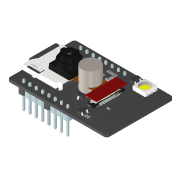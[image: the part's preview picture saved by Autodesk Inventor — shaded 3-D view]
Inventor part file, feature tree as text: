
AUTODESK INVENTOR PART (.ipt)
format: ipt  version: 2022 (Build 260153000, 153)  size: 4,575,232 bytes
history: native  units: mm
features: other x110, extrude x1, sketch x1, projected_geometry x1
ambient origin geometry x8: Origin, YZ Plane, XZ Plane, XY Plane, X Axis, Y Axis, Z Axis, Center Point
bodies: Volumenkörper1 (feature_tree), Volumenkörper2 (feature_tree), Volumenkörper3 (feature_tree), Volumenkörper4 (feature_tree), Volumenkörper5 (feature_tree), Volumenkörper6 (feature_tree), Volumenkörper7 (feature_tree), Volumenkörper8 (feature_tree), Volumenkörper9 (feature_tree), Volumenkörper10 (feature_tree), Volumenkörper11 (feature_tree), Volumenkörper12 (feature_tree), Volumenkörper13 (feature_tree), Volumenkörper14 (feature_tree), Volumenkörper15 (feature_tree), Volumenkörper16 (feature_tree), Volumenkörper17 (feature_tree), Volumenkörper18 (feature_tree), Volumenkörper19 (feature_tree), Volumenkörper20 (feature_tree), Volumenkörper21 (feature_tree), Volumenkörper22 (feature_tree), Volumenkörper23 (feature_tree), Volumenkörper24 (feature_tree), Volumenkörper25 (feature_tree), Volumenkörper26 (feature_tree), Volumenkörper27 (feature_tree), Volumenkörper28 (feature_tree), Volumenkörper29 (feature_tree), Volumenkörper30 (feature_tree), Volumenkörper31 (feature_tree), Volumenkörper32 (feature_tree), Volumenkörper33 (feature_tree), Volumenkörper34 (feature_tree), Volumenkörper35 (feature_tree), Volumenkörper36 (feature_tree), Volumenkörper37 (feature_tree), Volumenkörper38 (feature_tree), Volumenkörper39 (feature_tree), Volumenkörper40 (feature_tree), Volumenkörper41 (feature_tree), Volumenkörper42 (feature_tree), Volumenkörper43 (feature_tree), Volumenkörper44 (feature_tree), Volumenkörper45 (feature_tree), Volumenkörper46 (feature_tree), Volumenkörper47 (feature_tree), Volumenkörper48 (feature_tree), Volumenkörper49 (feature_tree), Volumenkörper50 (feature_tree), Volumenkörper51 (feature_tree), Volumenkörper52 (feature_tree), Volumenkörper53 (feature_tree), Volumenkörper54 (feature_tree), Volumenkörper55 (feature_tree), Volumenkörper56 (feature_tree), Volumenkörper57 (feature_tree), Volumenkörper58 (feature_tree), Volumenkörper59 (feature_tree), Volumenkörper60 (feature_tree), Volumenkörper61 (feature_tree), Volumenkörper62 (feature_tree), Volumenkörper63 (feature_tree), Volumenkörper64 (feature_tree), Volumenkörper65 (feature_tree), Volumenkörper66 (feature_tree), Volumenkörper67 (feature_tree), Volumenkörper68 (feature_tree), Volumenkörper69 (feature_tree), Volumenkörper70 (feature_tree), Volumenkörper71 (feature_tree), Volumenkörper72 (feature_tree), Volumenkörper73 (feature_tree), Volumenkörper74 (feature_tree), Volumenkörper75 (feature_tree), Volumenkörper76 (feature_tree), Volumenkörper77 (feature_tree), Volumenkörper78 (feature_tree), Volumenkörper79 (feature_tree), Volumenkörper80 (feature_tree), Volumenkörper81 (feature_tree), Volumenkörper82 (feature_tree), Volumenkörper83 (feature_tree), Volumenkörper84 (feature_tree), Volumenkörper85 (feature_tree), Volumenkörper86 (feature_tree), Volumenkörper87 (feature_tree), Volumenkörper88 (feature_tree), Volumenkörper89 (feature_tree), Volumenkörper90 (feature_tree), Volumenkörper91 (feature_tree), Volumenkörper92 (feature_tree), Volumenkörper93 (feature_tree), Volumenkörper94 (feature_tree), Volumenkörper95 (feature_tree), Volumenkörper96 (feature_tree), Volumenkörper97 (feature_tree), Volumenkörper98 (feature_tree), Volumenkörper99 (feature_tree), Volumenkörper100 (feature_tree), Volumenkörper101 (feature_tree), Volumenkörper102 (feature_tree), Volumenkörper103 (feature_tree), Volumenkörper104 (feature_tree), Volumenkörper105 (feature_tree), Volumenkörper106 (feature_tree), Volumenkörper107 (feature_tree), Volumenkörper108 (feature_tree), Volumenkörper109 (feature_tree), Volumenkörper110 (feature_tree)
feature tree (113):
  extrude  "Extrusion1"  Depth=10.0mm TaperAngle=0.0deg
  sketch  "Skizze1"  dims[d0=7.0mm d1=10.0mm d2=0.0mm]
  projected_geometry  "Projizierte Kontur1"
  other  "ESP3-CAM-1-solid1"
  other  "Pin Header 4 x 1 TH 2.54mm Pitch-1-solid1"
  other  "Pin Header 4 x 1 TH 2.54mm Pitch-1-solid2"
  other  "Pin Header 4 x 1 TH 2.54mm Pitch-1-solid3"
  other  "Pin Header 4 x 1 TH 2.54mm Pitch-1-solid4"
  other  "Pin Header 4 x 1 TH 2.54mm Pitch-1-solid5"
  other  "Pin Header 4 x 1 TH 2.54mm Pitch-1-solid6"
  other  "Pin Header 4 x 1 TH 2.54mm Pitch-1-solid7"
  other  "Pin Header 4 x 1 TH 2.54mm Pitch-1-solid8"
  other  "Pin Header 4 x 1 TH 2.54mm Pitch-2-solid1"
  other  "Pin Header 4 x 1 TH 2.54mm Pitch-2-solid2"
  other  "Pin Header 4 x 1 TH 2.54mm Pitch-2-solid3"
  other  "Pin Header 4 x 1 TH 2.54mm Pitch-2-solid4"
  other  "Pin Header 4 x 1 TH 2.54mm Pitch-2-solid5"
  other  "Pin Header 4 x 1 TH 2.54mm Pitch-2-solid6"
  other  "Pin Header 4 x 1 TH 2.54mm Pitch-2-solid7"
  other  "Pin Header 4 x 1 TH 2.54mm Pitch-2-solid8"
  other  "Pin Header 4 x 1 TH 2.54mm Pitch-3-solid1"
  other  "Pin Header 4 x 1 TH 2.54mm Pitch-3-solid2"
  other  "Pin Header 4 x 1 TH 2.54mm Pitch-3-solid3"
  other  "Pin Header 4 x 1 TH 2.54mm Pitch-3-solid4"
  other  "Pin Header 4 x 1 TH 2.54mm Pitch-3-solid5"
  other  "Pin Header 4 x 1 TH 2.54mm Pitch-3-solid6"
  other  "Pin Header 4 x 1 TH 2.54mm Pitch-3-solid7"
  other  "Pin Header 4 x 1 TH 2.54mm Pitch-3-solid8"
  other  "Pin Header 4 x 1 TH 2.54mm Pitch-4-solid1"
  other  "Pin Header 4 x 1 TH 2.54mm Pitch-4-solid2"
  other  "Pin Header 4 x 1 TH 2.54mm Pitch-4-solid3"
  other  "Pin Header 4 x 1 TH 2.54mm Pitch-4-solid4"
  other  "Pin Header 4 x 1 TH 2.54mm Pitch-4-solid5"
  other  "Pin Header 4 x 1 TH 2.54mm Pitch-4-solid6"
  other  "Pin Header 4 x 1 TH 2.54mm Pitch-4-solid7"
  other  "Pin Header 4 x 1 TH 2.54mm Pitch-4-solid8"
  other  "ESp32-WROOM-32U v3-1_u-1-solid1"
  other  "ESp32-WROOM-32U v3-1_u-1-solid2"
  other  "ESp32-WROOM-32U v3-1_u-1-solid3"
  other  "ESp32-WROOM-32U v3-1_u-1-solid4"
  other  "ESp32-WROOM-32U v3-1_u-1-solid5"
  other  "capacitor-CAPM-TANTB-YL-1-solid1"
  other  "capacitor-CAPM-TANTB-YL-1-solid2"
  other  "capacitor-CAPM-TANTB-YL-1-solid3"
  parser-record x1  (decoder bookkeeping rows leaked as tree rows — omitted from the tree; the rows remain in map.json)
  other  "nano - reg-1-solid1"
  other  "sop127p-6mm-8 v2-1_icbody-1-solid1"
  other  "sop127p-6mm-8 v2-1_Component5-1-solid1"
  other  "sop127p-6mm-8 v2-1_Component5-2-solid1"
  other  "sop127p-6mm-8 v2-1_Component5-3-solid1"
  other  "sop127p-6mm-8 v2-1_Component5-4-solid1"
  other  "sop127p-6mm-8 v2-1_Component5(Mirror)-1-solid1"
  other  "sop127p-6mm-8 v2-1_Component5(Mirror)-2-solid1"
  other  "sop127p-6mm-8 v2-1_Component5(Mirror)-3-solid1"
  other  "sop127p-6mm-8 v2-1_Component5(Mirror)-4-solid1"
  other  "SMD LED 0603-1_Fusion-1-solid1"
  other  "SMD LED 0603-1_Fillet-1-solid1"
  other  "resistor-NTC-0402-T0.6-1-solid1"
  other  "resistor-NTC-0402-T0.6-2-solid1"
  other  "resistor-NTC-0402-T0.6-3-solid1"
  other  "resistor-NTC-0805-T1.3-1-solid1"
  other  "resistor-NTC-0402-T0.6-4-solid1"
  other  "resistor-NTC-0402-T0.6-5-solid1"
  other  "resistor-NTC-0402-T0.6-6-solid1"
  other  "resistor-NTC-0402-T0.6-7-solid1"
  other  "smd-transistor-SOT23-3-1-solid1"
  other  "smd-transistor-SOT23-3-1-solid2"
  other  "smd-transistor-SOT23-3-1-solid3"
  other  "smd-transistor-SOT23-3-1-solid4"
  other  "smd-transistor-SOT23-3-2-solid1"
  other  "smd-transistor-SOT23-3-2-solid2"
  other  "smd-transistor-SOT23-3-2-solid3"
  other  "smd-transistor-SOT23-3-2-solid4"
  other  "resistor-NTC-0402-T0.6-8-solid1"
  other  "resistor-NTC-0402-T0.6-9-solid1"
  other  "resistor-NTC-0402-T0.6-10-solid1"
  other  "LED SMD 5050 White-1-solid1"
  other  "resistor-NTC-0402-T0.6-11-solid1"
  other  "resistor-NTC-0402-T0.6-12-solid1"
  other  "resistor-NTC-0402-T0.6-13-solid1"
  other  "resistor-NTC-0402-T0.6-14-solid1"
  other  "resistor-NTC-0402-T0.6-15-solid1"
  other  "resistor-NTC-0402-T0.6-16-solid1"
  other  "resistor-NTC-0402-T0.6-17-solid1"
  other  "capacitor-CAPC-0603-T0.9-BN-1-solid1"
  other  "resistor-NTC-0402-T0.6-18-solid1"
  other  "smd-transistor-SOT23-3-3-solid1"
  other  "smd-transistor-SOT23-3-3-solid2"
  other  "smd-transistor-SOT23-3-3-solid3"
  other  "smd-transistor-SOT23-3-3-solid4"
  other  "connector smd usl00-20l_p0-4_l12-6_w2-75-1-solid1"
  other  "resistor-NTC-0402-T0.6-19-solid1"
  other  "resistor-NTC-0402-T0.6-20-solid1"
  other  "smd-transistor-SOT23-3-4-solid1"
  other  "smd-transistor-SOT23-3-4-solid2"
  other  "smd-transistor-SOT23-3-4-solid3"
  other  "smd-transistor-SOT23-3-4-solid4"
  other  "MicroSD Slot-1_sdreader-1-solid1"
  other  "Micro SD-Card-1-solid1"
  other  "Micro SD-Card-1-solid2"
  other  "Micro SD-Card-1-solid3"
  other  "Micro SD-Card-1-solid4"
  other  "Micro SD-Card-1-solid5"
  other  "Micro SD-Card-1-solid6"
  other  "Micro SD-Card-1-solid7"
  other  "Micro SD-Card-1-solid8"
  other  "Micro SD-Card-1-solid9"
  other  "camera for ESP32-1_User Library-ov9655_ov9655_flex_pcb-1-solid1"
  other  "camera for ESP32-1_User Library-ov9655_ov9655_flex_reinf-1-solid1"
  other  "camera for ESP32-1_User Library-ov9655_ov9655_back_panel-1-solid1"
  other  "camera for ESP32-1_User Library-ov9655_ov9655_body-1-solid1"
  other  "camera for ESP32-1_User Library-ov9655_ov9655_lens-1-solid1"
  other  "Boss-Extrude1"
